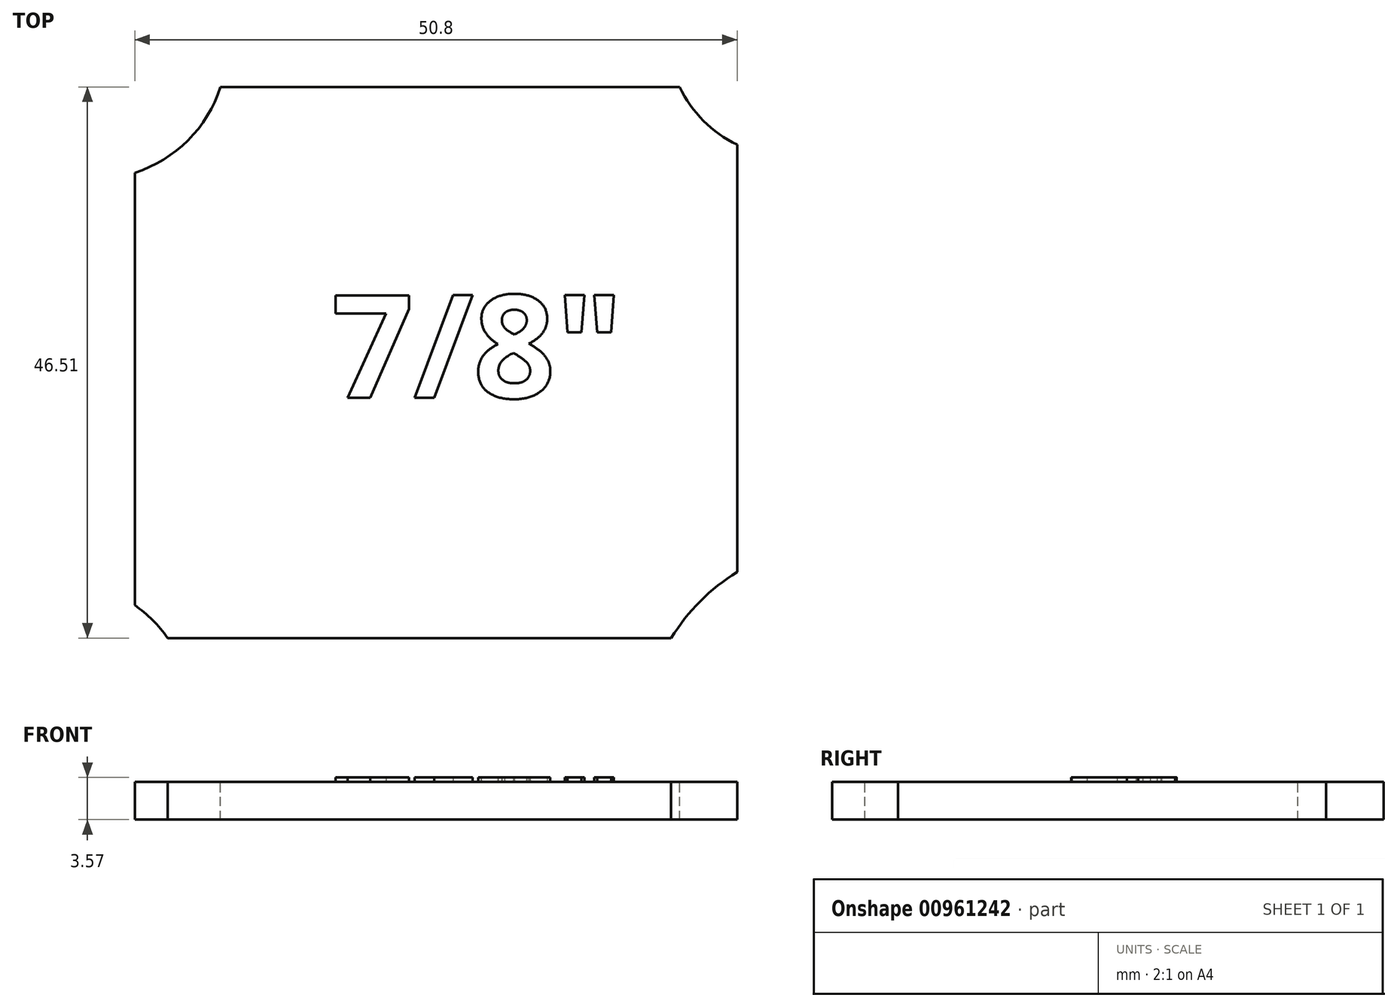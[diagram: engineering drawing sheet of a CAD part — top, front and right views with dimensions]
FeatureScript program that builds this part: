
annotation { "Feature Type Name" : "Feature", "Feature Type Description" : "" }
export const myFeature = defineFeature(function(context is Context, id is Id, definition is map)
    precondition{}
    {
        {
            var Q0;
            Q0=qCreatedBy(makeId("Top.planeOp"),FACE);
            var sketch = newSketch(context, id + "F0", { "sketchPlane" : qUnion([Q0])});
            skLineSegment(sketch, "E0.bottom", {"start": v(-76.58, -34.06) * mm, "end": v(-34.12, -34.06) * mm});
            skLineSegment(sketch, "E0.top", {"start": v(-72.13, 12.45) * mm, "end": v(-34.9, 12.45) * mm});
            skLineSegment(sketch, "E0.left", {"start": v(-79.35, -31.29) * mm, "end": v(-79.35, 5.22) * mm});
            skLineSegment(sketch, "E0.right", {"start": v(-28.55, -28.5) * mm, "end": v(-28.55, 6.1) * mm});
            skArc(sketch, "E1", {"start": v(-76.58, -34.06) * mm, "mid": v(-77.85, -32.55) * mm, "end": v(-79.35, -31.29) * mm});
            skLineSegment(sketch, "E2", {"start": v(-79.35, -34.06) * mm, "end": v(-85.7, -34.06) * mm, "construction": true});
            skLineSegment(sketch, "E3", {"start": v(-85.7, -34.06) * mm, "end": v(-85.7, -40.4) * mm, "construction": true});
            skPoint(sketch, "E4.visualSharp", {"position": v(-28.55, 12.45) * mm});
            skArc(sketch, "E5", {"start": v(-79.35, 5.22) * mm, "mid": v(-74.86, 7.96) * mm, "end": v(-72.13, 12.45) * mm});
            skLineSegment(sketch, "E6", {"start": v(-82.72, 15.81) * mm, "end": v(-79.35, 12.45) * mm, "construction": true});
            skArc(sketch, "E7", {"start": v(-33.4, 12.45) * mm, "mid": v(-31.4, 9.6) * mm, "end": v(-28.55, 7.6) * mm});
            skLineSegment(sketch, "E8", {"start": v(-34.9, 12.45) * mm, "end": v(-33.4, 12.45) * mm});
            skLineSegment(sketch, "E9", {"start": v(-28.55, 6.1) * mm, "end": v(-28.55, 7.6) * mm});
            skLineSegment(sketch, "E10", {"start": v(-28.55, 12.45) * mm, "end": v(-24.06, 16.94) * mm, "construction": true});
            skArc(sketch, "E11", {"start": v(-28.55, -28.5) * mm, "mid": v(-31.66, -30.95) * mm, "end": v(-34.12, -34.06) * mm});
            skLineSegment(sketch, "E12", {"start": v(-28.55, -34.06) * mm, "end": v(-19.57, -43.04) * mm, "construction": true});
            skSolve(sketch);
        }
        {
            var Q0;
            Q0 = qSketchRegion(id + "F0", true);
            extrude(context, id + "F1", {"entities" : qUnion([Q0]), "endBound" : BoundingType.SYMMETRIC, "oppositeDirection" : true, "depth" : 3.17 * mm, "offsetDistance" : 25.4 * mm});
        }
        {
            var Q0;
            Q0=makeQuery(id+"F1.opExtrude","CAP_FACE",FACE,{"disambiguationData":[OSD([sQuery(id+"F0.wireOp",EDGE,"E0.bottom"),sQuery(id+"F0.wireOp",EDGE,"E0.top"),sQuery(id+"F0.wireOp",EDGE,"E0.left"),sQuery(id+"F0.wireOp",EDGE,"E0.right"),sQuery(id+"F0.wireOp",EDGE,"E1"),sQuery(id+"F0.wireOp",EDGE,"86JFj3BK-gVwY-y3ax-lvxs-ULLyLjZGH39d"),sQuery(id+"F0.wireOp",EDGE,"E4.filletArc"),sQuery(id+"F0.wireOp",EDGE,"E5")])],"isStart":true});
            var sketch = newSketch(context, id + "F2", { "sketchPlane" : qUnion([Q0])});
            skText(sketch, "E13", { "text": "7/8\"", "fontName": "OpenSans-Bold.ttf"});
            const initialGuessF2  = {"E13": [-0.06276, -0.01378, 1, 0, 0.00874]};
            skSetInitialGuess(sketch, initialGuessF2);
            skSolve(sketch);
        }
        {
            var Q0;
            Q0 = qSketchRegion(id + "F2", true);
            extrude(context, id + "F3", {"entities" : qUnion([Q0]), "operationType" : NewBodyOperationType.ADD, "depth" : 0.4 * mm, "offsetDistance" : 25.4 * mm});
        }
    });
